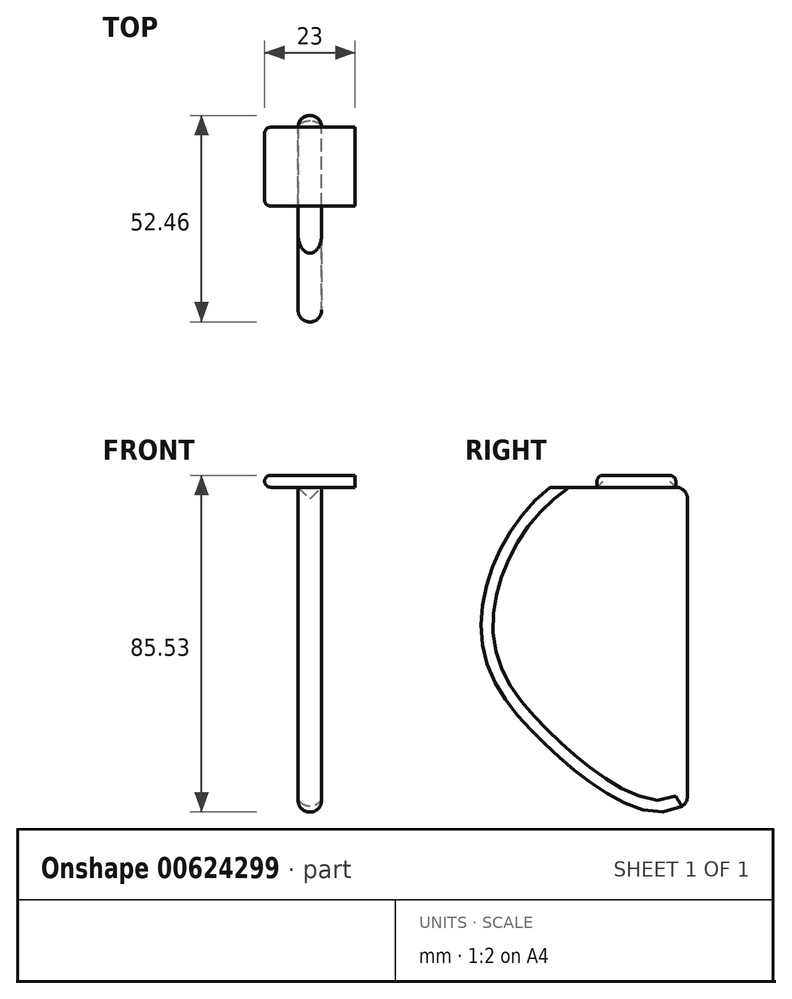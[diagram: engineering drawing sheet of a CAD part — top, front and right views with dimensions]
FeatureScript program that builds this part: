
annotation { "Feature Type Name" : "Feature", "Feature Type Description" : "" }
export const myFeature = defineFeature(function(context is Context, id is Id, definition is map)
    precondition{}
    {
        {
            var Q0;
            Q0=qCreatedBy(makeId("Right.planeOp"),FACE);
            var sketch = newSketch(context, id + "F0", { "sketchPlane" : qUnion([Q0])});
            skLineSegment(sketch, "E0", {"start": v(-21.83, 25.34) * mm, "end": v(13.17, 25.34) * mm});
            skLineSegment(sketch, "E1", {"start": v(13.17, 25.34) * mm, "end": v(13.17, -54.66) * mm});
            skFitSpline(sketch, "E2", {"points": [v(-21.83, 25.34) * mm, v(-39.25, -11.6) * mm, v(-21.83, -41.04) * mm, v(13.17, -54.66) * mm, v(13.17, 25.34) * mm, v(-21.83, 25.34) * mm]});
            skSolve(sketch);
        }
        {
            var Q0;
            Q0=makeQuery(id+"F0.imprint","IMPRINT",FACE,{"disambiguationData":[TD([[makeQuery(id+"F0.imprint","IMPRINT",EDGE,{"derivedFrom":sQuery(id+"F0.wireOp",EDGE,"E0")}),-1.0]])]});
            extrude(context, id + "F1", {"entities" : qUnion([Q0]), "depth" : 6 * mm, "offsetDistance" : 25 * mm});
        }
        {
            var Q0;
            Q0=makeQuery(id+"F1.opExtrude","CAP_EDGE",EDGE,{"disambiguationData":[OSD([sQuery(id+"F0.wireOp",EDGE,"E1")])],"isStart":false});
            var Q1;
            Q1=makeQuery(id+"F1.opExtrude","SWEPT_FACE",FACE,{"disambiguationData":[OSD([sQuery(id+"F0.wireOp",EDGE,"E1")])]});
            fillet(context, id + "F2", {"entities" : qUnion([Q0, Q1]), "radius" : 3 * mm, "tangentPropagation" : true, "allowEdgeOverflow" : false});
        }
        {
            var Q0;
            Q0=makeQuery(id+"F1.opExtrude","CAP_EDGE",EDGE,{"disambiguationData":[OSD([sQuery(id+"F0.wireOp",EDGE,"E2")])],"isStart":false});
            var Q1;
            Q1=makeQuery(id+"F1.opExtrude","CAP_EDGE",EDGE,{"disambiguationData":[OSD([sQuery(id+"F0.wireOp",EDGE,"E2")])],"isStart":true});
            fillet(context, id + "F3", {"entities" : qUnion([Q0, Q1]), "radius" : 3 * mm, "tangentPropagation" : true, "allowEdgeOverflow" : false});
        }
        {
            var Q0;
            Q0=makeQuery(id+"F1.opExtrude","SWEPT_FACE",FACE,{"disambiguationData":[OSD([sQuery(id+"F0.wireOp",EDGE,"E0")])]});
            var sketch = newSketch(context, id + "F4", { "sketchPlane" : qUnion([Q0])});
            skLineSegment(sketch, "E3.bottom", {"start": v(0, 10.17) * mm, "end": v(-8.5, 10.17) * mm});
            skLineSegment(sketch, "E3.top", {"start": v(0, -9.83) * mm, "end": v(-8.5, -9.83) * mm});
            skLineSegment(sketch, "E3.left", {"start": v(0, 10.17) * mm, "end": v(0, -9.83) * mm});
            skLineSegment(sketch, "E3.right", {"start": v(-8.5, 10.17) * mm, "end": v(-8.5, -9.83) * mm});
            skLineSegment(sketch, "E4.bottom", {"start": v(6, 10.17) * mm, "end": v(14.5, 10.17) * mm});
            skLineSegment(sketch, "E4.top", {"start": v(6, -9.83) * mm, "end": v(14.5, -9.83) * mm});
            skLineSegment(sketch, "E4.left", {"start": v(6, 10.17) * mm, "end": v(6, -9.83) * mm});
            skLineSegment(sketch, "E4.right", {"start": v(14.5, 10.17) * mm, "end": v(14.5, -9.83) * mm});
            skLineSegment(sketch, "E5.bottom", {"start": v(14.5, 10.17) * mm, "end": v(-8.5, 10.17) * mm});
            skLineSegment(sketch, "E5.top", {"start": v(14.5, -9.83) * mm, "end": v(-8.5, -9.83) * mm});
            skSolve(sketch);
        }
        {
            var Q0;
            {var subQ0=sQuery(id+"F4.wireOp",EDGE,"E3.left");Q0=makeQuery(id+"F4.imprint","IMPRINT",FACE,{"disambiguationData":[TD([[makeQuery(id+"F4.imprint","IMPRINT",EDGE,{"derivedFrom":subQ0}),1.0]])]});}
            var Q1;
            {var subQ0=sQuery(id+"F4.wireOp",EDGE,"E3.left");Q1=makeQuery(id+"F4.imprint","IMPRINT",FACE,{"disambiguationData":[TD([[makeQuery(id+"F4.imprint","IMPRINT",EDGE,{"derivedFrom":subQ0}),-1.0]])]});}
            var Q2;
            {var subQ0=sQuery(id+"F4.wireOp",EDGE,"E4.left");Q2=makeQuery(id+"F4.imprint","IMPRINT",FACE,{"disambiguationData":[TD([[makeQuery(id+"F4.imprint","IMPRINT",EDGE,{"derivedFrom":subQ0}),-1.0]])]});}
            extrude(context, id + "F5", {"entities" : qUnion([Q0, Q1, Q2]), "operationType" : NewBodyOperationType.ADD, "depth" : 3 * mm, "offsetDistance" : 25 * mm});
        }
        {
            var Q0;
            Q0=makeQuery(id+"F5.opExtrude","SWEPT_FACE",FACE,{"disambiguationData":[OSD([sQuery(id+"F4.wireOp",EDGE,"E3.right")])]});
            var Q1;
            Q1=makeQuery(id+"F5.opExtrude","SWEPT_FACE",FACE,{"disambiguationData":[OSD([sQuery(id+"F4.wireOp",EDGE,"E4.right")])]});
            var Q2;
            Q2=makeQuery(id+"F5.opExtrude","CAP_EDGE",EDGE,{"disambiguationData":[OSD([sQuery(id+"F4.wireOp",EDGE,"E5.top")])],"isStart":false});
            var Q3;
            Q3=makeQuery(id+"F5.opExtrude","CAP_EDGE",EDGE,{"disambiguationData":[OSD([sQuery(id+"F4.wireOp",EDGE,"E5.bottom")])],"isStart":false});
            fillet(context, id + "F6", {"entities" : qUnion([Q0, Q1, Q2, Q3]), "radius" : 1.5 * mm, "tangentPropagation" : true, "allowEdgeOverflow" : false});
        }
    });
